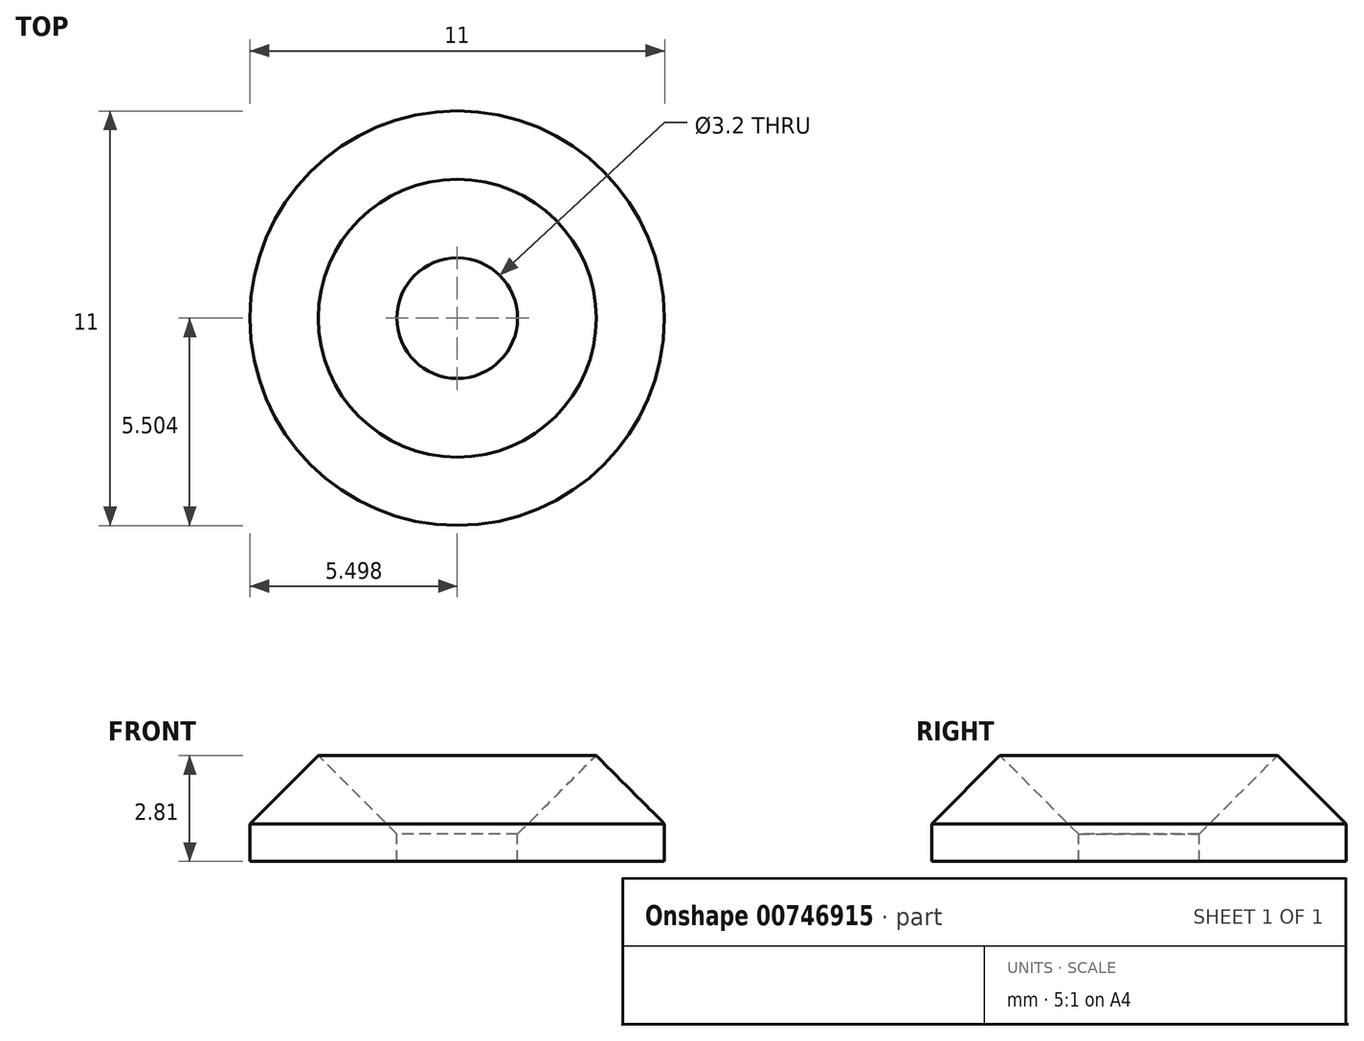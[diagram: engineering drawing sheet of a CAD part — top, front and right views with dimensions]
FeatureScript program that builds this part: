
annotation { "Feature Type Name" : "Feature", "Feature Type Description" : "" }
export const myFeature = defineFeature(function(context is Context, id is Id, definition is map)
    precondition{}
    {
        {
            var Q0;
            Q0=qCreatedBy(makeId("Top.planeOp"),FACE);
            var sketch = newSketch(context, id + "F0", { "sketchPlane" : qUnion([Q0])});
            skCircle(sketch, "E0", {"center": v(-42.96, 14.7) * mm, "radius": 5.5 * mm});
            skSolve(sketch);
        }
        {
            var Q0;
            Q0 = qSketchRegion(id + "F0", true);
            extrude(context, id + "F1", {"entities" : qUnion([Q0]), "depth" : 3 * mm, "offsetDistance" : 25 * mm});
        }
        {
            var Q0;
            Q0=makeQuery(id+"F1.opExtrude","CAP_FACE",FACE,{"disambiguationData":[OSD([sQuery(id+"F0.wireOp",EDGE,"E0")])],"isStart":false});
            var sketch = newSketch(context, id + "F2", { "sketchPlane" : qUnion([Q0])});
            skCircle(sketch, "E1", {"center": v(-42.96, 14.7) * mm, "radius": 0.95 * mm});
            skSolve(sketch);
        }
        {
            var Q0;
            Q0=sQuery(id+"F2.wireOp",VERTEX,"E1.center");
            var Q1;
            Q1=makeQuery(id+"F1.opExtrude","SWEPT_BODY",BODY,{"disambiguationData":[OSD([sQuery(id+"F0.wireOp",EDGE,"E0")])]});
            hole(context, id + "F3", {"style" : HoleStyle.C_SINK, "endStyle" : HoleEndStyle.BLIND, "holeDiameter" : 3.2 * mm, "cSinkDiameter" : 7.75 * mm, "cSinkAngle" : 90 * degree, "majorDiameter" : 5 * mm, "holeDepth" : 12 * mm, "tappedDepth" : 12 * mm, "tapClearance" : 3, "locations" : qUnion([Q0]), "scope" : qUnion([Q1])});
        }
        {
            var Q0;
            Q0=makeQuery(id+"F1.opExtrude","CAP_EDGE",EDGE,{"disambiguationData":[OSD([sQuery(id+"F0.wireOp",EDGE,"E0")])],"isStart":false});
            chamfer(context, id + "F4", {"entities" : qUnion([Q0]), "width" : 2 * mm, "tangentPropagation" : true});
        }
    });
